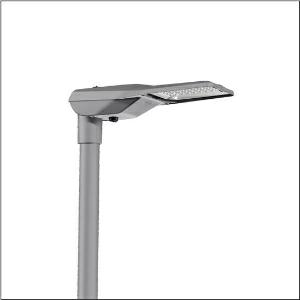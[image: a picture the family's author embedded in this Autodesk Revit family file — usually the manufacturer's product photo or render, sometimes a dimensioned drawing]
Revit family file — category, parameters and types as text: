
# Revit family: streetlight_sl_21_iq_mini___st1_0a_5xe2d21y08hb_5d36
name_source: partatom
category: Lighting Fixtures
units: mm (PartAtom-declared; Revit-internal decimal feet)

## family parameters
Cut with Voids When Loaded = No
Host = Face
Light Source = No
Part Type = Normal
Room Calculation Point = No
Round Connector Dimension = Use Diameter
Shared = No

## types (1)
- --- (1 x LED, 7820 lm, 71 W, 2200K)
    Apparent Load = 71 VA
    CIE Flux Codes = 37 72 97 100 100
    Color Rendering = 70
    Color Temperature = 2200K
    Default Elevation = 1800 mm
    Description = Streetlight SL 21 iQ mini, mast luminaire, primary light control with lens, of PMMA, primary optical cover: cover, of toughened safety glass, transparent, light distribution: ST1.0a, light emission: direct distribution, primary light characteristic: asymmetric, installation type: post-top, side-entry, LED, High Power LED, rated luminous flux: 7.820lm, luminous efficacy: 110lm/W, light colour: 722, colour temperature: 2200K, control gear: iQ-Street Remote, D4i with power reduction, control: pre-setting: logarithmic dimming characteristic, Street-Remote, Auto-Match, Temp-Guard, Lumen-Switch, Night-Set, Smart-Wire, Light-Fading, Desk-Remote (wireless, voltage-free reading and setting of iQ features in the workshop via application-optimized NFC function/RFID function), optimised constant luminous flux control (CLO 2.0), mains connection: 220..240V, AC, 50/60Hz, start of lifetime: 71W, end of service life: 75W, reduction: 30W, luminaire housing, of diecast aluminium, powder-coated, Siteco® metallic grey (DB 702S), corrosivity category C5 high according to DIN EN ISO 12944, please order mast flange separately, inclination adjustable: 0°, 5°, 10°, 15°, sealing non-destructively replaceable, multi-level sealing system, length: 628mm, width: 235mm, height: 110mm, mast flange for spigot size: 42mm (side-entry): 5XC10008XM4, 60/48mm (side-entry/post-top): 5XC10108XM2, 76/60mm (side-entry/post-top): 5XC10108XM1, mounting height: 4..8m, Smart Interface below and above, protection rating (complete): IP66, insulation class (complete): insulation class II (safety insulation), certification: CE, ENEC, ENEC+, VDE, impact resistance: IK10, permissible operating ambient temperature for outdoor applications: -40..+50°C, standard-compliant lighting for roads and squares, packaging unit: 1 piece

Light Distribution: ST1.0a
    Height = 110 mm
    Lamp = 1 x LED
    Lamp Light Flux = 7820 lm
    Lamp Power = 71 W
    Lamp count = 1
    Length = 625 mm
    Luminous efficacy = 110 lm/W
    Manufacturer = Siteco
    ModVariant = No
    Model = 5XE2D21Y08HB
    Number of Poles = 1
    OnlyDefault = Yes
    Power Factor = 1
    Product Name = Streetlight SL 21 iQ mini | ST1.0a
    Product group = mast luminaire | pylon top
    ProductGroupID = 6100
    Protection Class = Protection class II
    Protection Degree = IP 66
    RLX_Detail_Level = 1
    RLX_Emergency_Light_Flux = 0 lm
    RLX_Emergency_Type = 0
    RLX_Emergency_Type_DB = No
    RlxData = <blob elided: 92441 chars, md5=712aaff6>
    Socket = socket
    Standby Power = 0 W
    System Light Flux = 7820 lm
    System Power = 71 W
    Type Comments = factory setting: luminous flux: 100 % | dim-lin: 254 | 716 mA
    Type Image = l_1003514.jpg
    URL = http://relux.com
    VarID = @adj_118937
    Voltage = 0 V
    Weight = 0.00 kg
    Width = 234 mm

## geometry (parser evidence)
native form markers: Blend x4, Sweep x10
no freeform markers — native parametric forms only
